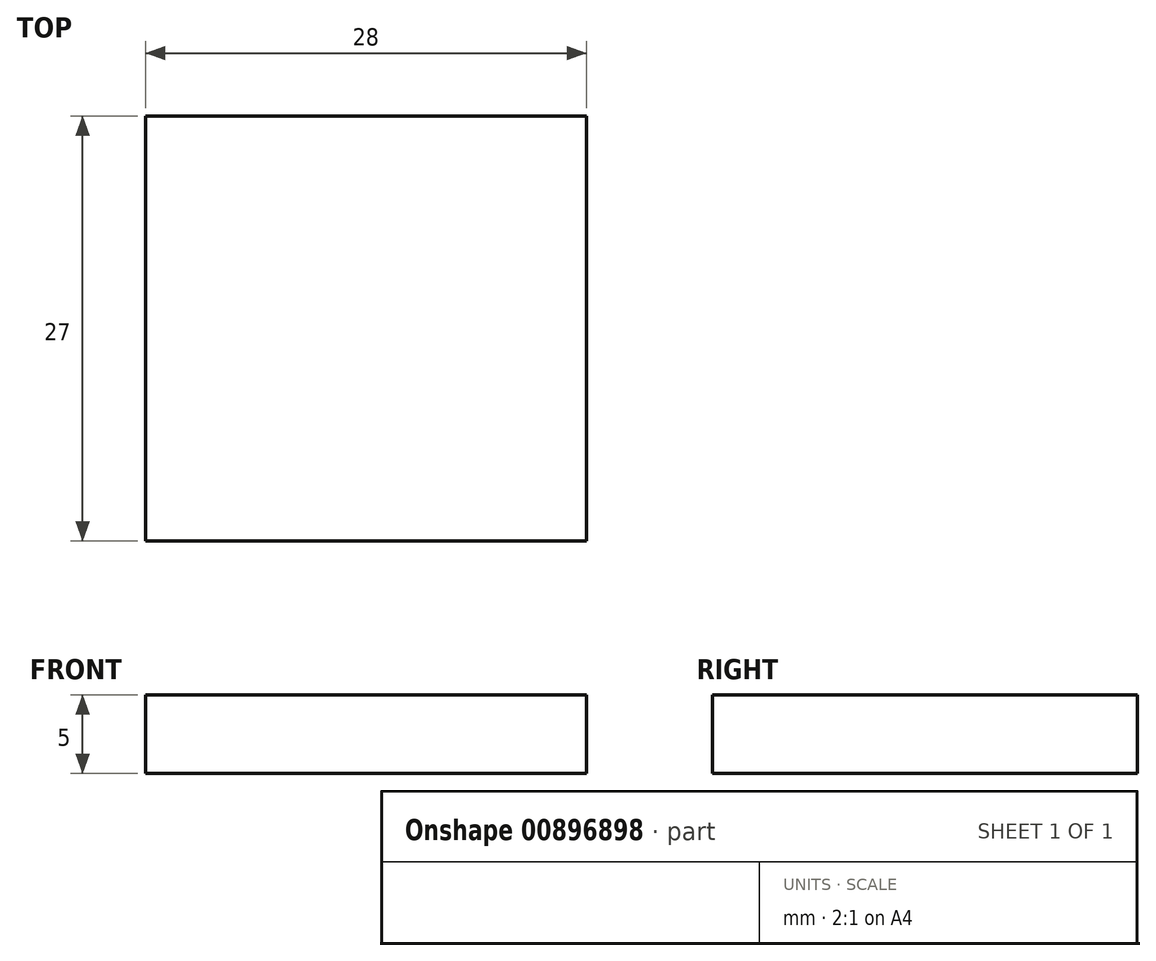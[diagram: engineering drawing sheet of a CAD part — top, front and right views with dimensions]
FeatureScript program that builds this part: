
annotation { "Feature Type Name" : "Feature", "Feature Type Description" : "" }
export const myFeature = defineFeature(function(context is Context, id is Id, definition is map)
    precondition{}
    {
        {
            var Q0;
            Q0=qCreatedBy(makeId("Top.planeOp"),FACE);
            var sketch = newSketch(context, id + "F0", { "sketchPlane" : qUnion([Q0])});
            skLineSegment(sketch, "E0.bottom", {"start": v(14, 13.5) * mm, "end": v(-14, 13.5) * mm});
            skLineSegment(sketch, "E0.top", {"start": v(14, -13.5) * mm, "end": v(-14, -13.5) * mm});
            skLineSegment(sketch, "E0.left", {"start": v(14, 13.5) * mm, "end": v(14, -13.5) * mm});
            skLineSegment(sketch, "E0.right", {"start": v(-14, 13.5) * mm, "end": v(-14, -13.5) * mm});
            skPoint(sketch, "E0.middle", {"position": v(0, 0) * mm});
            skSolve(sketch);
        }
        {
            var Q0;
            Q0=qSketchRegion(id+"F0",true);
            extrude(context, id + "F1", {"entities" : qUnion([Q0]), "depth" : 5 * mm, "offsetDistance" : 25 * mm});
        }
    });
